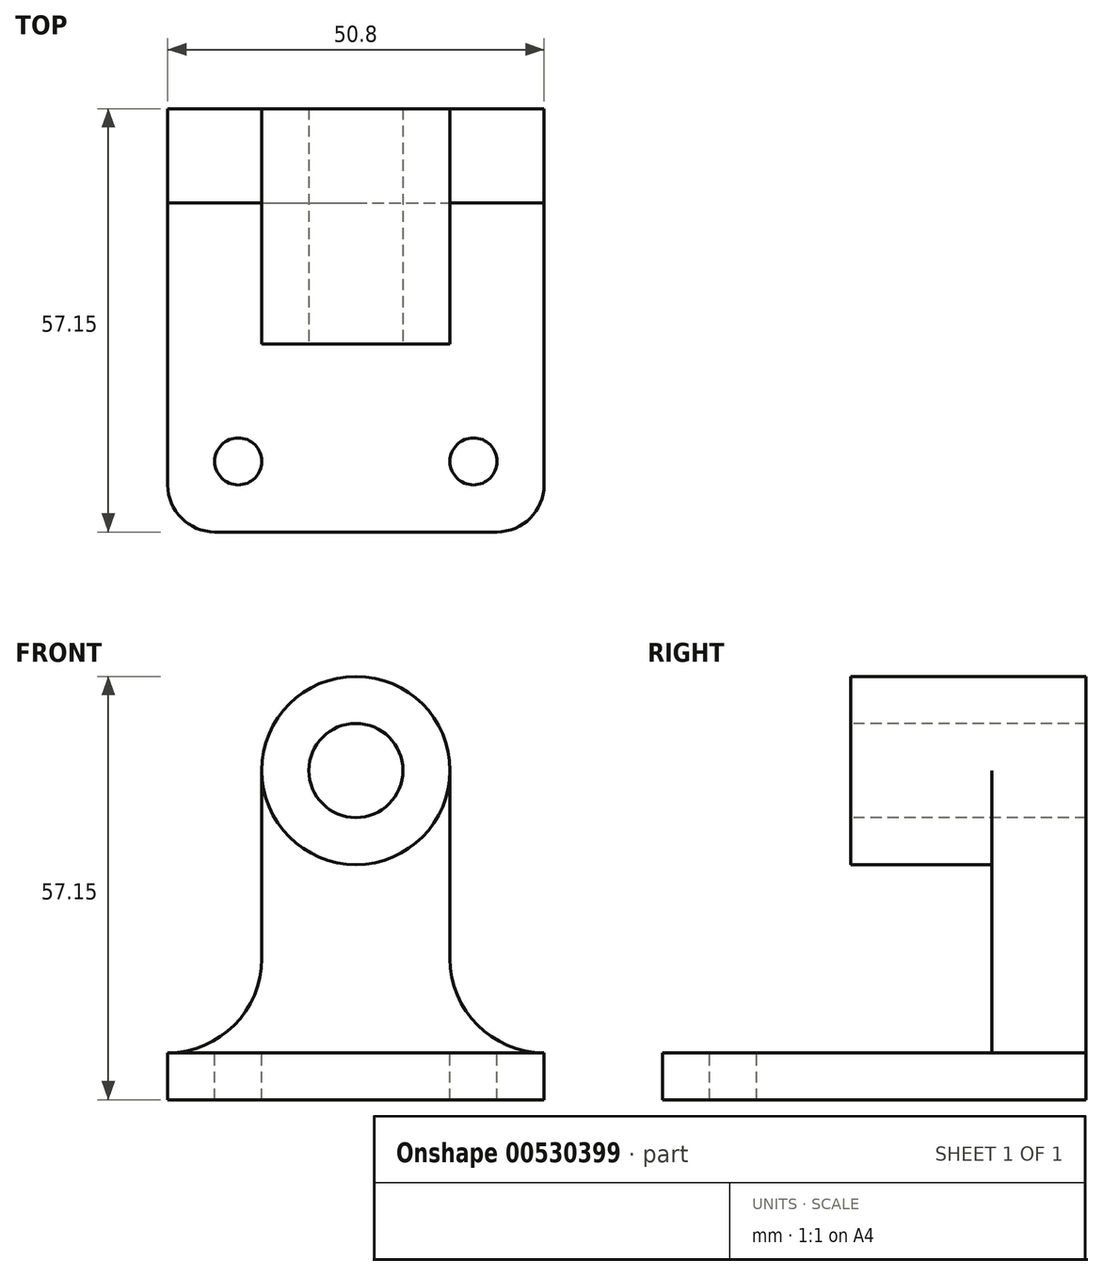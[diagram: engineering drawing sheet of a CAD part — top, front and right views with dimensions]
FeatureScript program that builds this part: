
annotation { "Feature Type Name" : "Feature", "Feature Type Description" : "" }
export const myFeature = defineFeature(function(context is Context, id is Id, definition is map)
    precondition{}
    {
        {
            var Q0;
            Q0=qCreatedBy(makeId("Front.planeOp"),FACE);
            var sketch = newSketch(context, id + "F0", { "sketchPlane" : qUnion([Q0])});
            skLineSegment(sketch, "E0.bottom", {"start": v(-66.92, 57.15) * mm, "end": v(-16.12, 57.15) * mm});
            skLineSegment(sketch, "E0.top", {"start": v(-66.92, 0) * mm, "end": v(-16.12, 0) * mm});
            skLineSegment(sketch, "E0.left", {"start": v(-66.92, 57.15) * mm, "end": v(-66.92, 0) * mm});
            skLineSegment(sketch, "E0.right", {"start": v(-16.12, 57.15) * mm, "end": v(-16.12, 0) * mm});
            skLineSegment(sketch, "E1", {"start": v(-66.92, 0) * mm, "end": v(-66.92, 6.35) * mm});
            skLineSegment(sketch, "E2", {"start": v(-66.92, 6.35) * mm, "end": v(-16.12, 6.35) * mm});
            skLineSegment(sketch, "E3", {"start": v(-16.12, 6.35) * mm, "end": v(-16.12, 0) * mm});
            skLineSegment(sketch, "E4", {"start": v(-66.92, 6.35) * mm, "end": v(-58.15, 6.35) * mm});
            skLineSegment(sketch, "E5", {"start": v(-58.15, 6.35) * mm, "end": v(-58.15, 57.15) * mm});
            skLineSegment(sketch, "E6", {"start": v(-58.15, 57.15) * mm, "end": v(-30.55, 57.15) * mm});
            skLineSegment(sketch, "E7", {"start": v(-30.55, 57.15) * mm, "end": v(-30.55, 6.35) * mm});
            skLineSegment(sketch, "E8", {"start": v(-30.55, 6.35) * mm, "end": v(-16.12, 6.35) * mm});
            skSolve(sketch);
        }
        {
            var Q0;
            Q0=makeQuery(id+"F0.imprint","IMPRINT",FACE,{"disambiguationData":[TD([[makeQuery(id+"F0.imprint","IMPRINT",EDGE,{"derivedFrom":sQuery(id+"F0.wireOp",EDGE,"E2")}),1.0]])]});
            var Q1;
            {var subQ0=sQuery(id+"F0.wireOp",EDGE,"E0.left");Q1=makeQuery(id+"F0.imprint","IMPRINT",FACE,{"disambiguationData":[TD([[makeQuery(id+"F0.imprint","IMPRINT",EDGE,{"derivedFrom":subQ0}),1.0]])]});}
            var Q2;
            {var subQ0=sQuery(id+"F0.wireOp",EDGE,"E0.right");Q2=makeQuery(id+"F0.imprint","IMPRINT",FACE,{"disambiguationData":[TD([[makeQuery(id+"F0.imprint","IMPRINT",EDGE,{"derivedFrom":subQ0}),-1.0]])]});}
            var Q3;
            Q3=makeQuery(id+"F0.imprint","IMPRINT",FACE,{"disambiguationData":[TD([[makeQuery(id+"F0.imprint","IMPRINT",EDGE,{"derivedFrom":sQuery(id+"F0.wireOp",EDGE,"E0.top")}),1.0]])]});
            extrude(context, id + "F1", {"entities" : qUnion([Q0, Q1, Q2, Q3]), "depth" : 31.75 * mm, "offsetDistance" : 25.4 * mm});
        }
        {
            var Q0;
            Q0=makeQuery(id+"F1.opExtrude","CAP_FACE",FACE,{"disambiguationData":[OSD([sQuery(id+"F0.wireOp",EDGE,"E0.bottom"),sQuery(id+"F0.wireOp",EDGE,"E0.top"),sQuery(id+"F0.wireOp",EDGE,"E0.left"),sQuery(id+"F0.wireOp",EDGE,"E0.right"),sQuery(id+"F0.wireOp",EDGE,"E1"),sQuery(id+"F0.wireOp",EDGE,"E3"),sQuery(id+"F0.wireOp",EDGE,"E6")])],"isStart":false});
            var sketch = newSketch(context, id + "F2", { "sketchPlane" : qUnion([Q0])});
            skLineSegment(sketch, "E9", {"start": v(-66.92, 0) * mm, "end": v(-66.92, 6.35) * mm});
            skLineSegment(sketch, "E10", {"start": v(-66.92, 6.35) * mm, "end": v(-16.12, 6.35) * mm});
            skLineSegment(sketch, "E11", {"start": v(-16.12, 6.35) * mm, "end": v(-16.12, 0) * mm});
            skLineSegment(sketch, "E12", {"start": v(-16.12, 0) * mm, "end": v(-66.92, 0) * mm});
            skLineSegment(sketch, "E13", {"start": v(-66.92, 6.35) * mm, "end": v(-66.92, 44.45) * mm});
            skLineSegment(sketch, "E14", {"start": v(-16.12, 44.45) * mm, "end": v(-16.12, 6.35) * mm});
            skCircle(sketch, "E15", {"center": v(-41.52, 44.45) * mm, "radius": 12.7 * mm});
            skCircle(sketch, "E16", {"center": v(-41.52, 44.45) * mm, "radius": 6.35 * mm});
            skLineSegment(sketch, "E17", {"start": v(-28.82, 44.45) * mm, "end": v(-28.82, 6.35) * mm});
            skLineSegment(sketch, "E18", {"start": v(-28.82, 6.35) * mm, "end": v(-16.12, 6.35) * mm});
            skLineSegment(sketch, "E19", {"start": v(-16.12, 44.45) * mm, "end": v(-28.82, 44.45) * mm});
            skLineSegment(sketch, "E20", {"start": v(-54.22, 44.45) * mm, "end": v(-54.22, 6.35) * mm});
            skLineSegment(sketch, "E21", {"start": v(-54.22, 6.35) * mm, "end": v(-66.92, 6.35) * mm});
            skLineSegment(sketch, "E22", {"start": v(-66.92, 44.45) * mm, "end": v(-54.22, 44.45) * mm});
            skLineSegment(sketch, "E23", {"start": v(-28.82, 44.45) * mm, "end": v(-16.12, 44.45) * mm});
            skLineSegment(sketch, "E24", {"start": v(-54.22, 44.45) * mm, "end": v(-28.82, 44.45) * mm});
            skLineSegment(sketch, "E25", {"start": v(-28.82, 44.45) * mm, "end": v(-28.82, 57.15) * mm});
            skLineSegment(sketch, "E26", {"start": v(-54.22, 44.45) * mm, "end": v(-54.22, 57.15) * mm});
            skLineSegment(sketch, "E27", {"start": v(-54.22, 57.15) * mm, "end": v(-66.92, 57.15) * mm});
            skLineSegment(sketch, "E28", {"start": v(-66.92, 57.15) * mm, "end": v(-66.92, 44.45) * mm});
            skLineSegment(sketch, "E29", {"start": v(-28.82, 57.15) * mm, "end": v(-16.12, 57.15) * mm});
            skLineSegment(sketch, "E30", {"start": v(-16.12, 57.15) * mm, "end": v(-16.12, 44.45) * mm});
            skSolve(sketch);
        }
        {
            var Q0;
            {var subQ3=sQuery(id+"F2.wireOp",EDGE,"E22");Q0=makeQuery(id+"F2.imprint","IMPRINT",FACE,{"disambiguationData":[TD([[makeQuery(id+"F2.imprint","IMPRINT",EDGE,{"derivedFrom":subQ3}),1.0]])]});}
            var Q1;
            {var subQ0=sQuery(id+"F2.wireOp",EDGE,"E26");var subQ1=sQuery(id+"F2.wireOp",EDGE,"E15");var subQ2=makeQuery(id+"F2.imprint","INTERSECT",VERTEX,{"derivedFrom":[subQ1,subQ0]});Q1=makeQuery(id+"F2.imprint","IMPRINT",FACE,{"disambiguationData":[TD([[makeQuery(id+"F2.imprint","IMPRINT",EDGE,{"disambiguationData":[TD([[subQ2,1.0]])],"derivedFrom":subQ1}),-1.0]])]});}
            var Q2;
            {var subQ0=sQuery(id+"F2.wireOp",EDGE,"E25");var subQ1=sQuery(id+"F2.wireOp",EDGE,"E15");var subQ2=makeQuery(id+"F2.imprint","INTERSECT",VERTEX,{"derivedFrom":[subQ1,subQ0]});Q2=makeQuery(id+"F2.imprint","IMPRINT",FACE,{"disambiguationData":[TD([[makeQuery(id+"F2.imprint","IMPRINT",EDGE,{"disambiguationData":[TD([[subQ2,-1.0]])],"derivedFrom":subQ1}),-1.0]])]});}
            var Q3;
            {var subQ3=sQuery(id+"F2.wireOp",EDGE,"E23");Q3=makeQuery(id+"F2.imprint","IMPRINT",FACE,{"disambiguationData":[TD([[makeQuery(id+"F2.imprint","IMPRINT",EDGE,{"derivedFrom":subQ3}),1.0]])]});}
            extrude(context, id + "F3", {"entities" : qUnion([Q0, Q1, Q2, Q3]), "operationType" : NewBodyOperationType.REMOVE, "endBound" : BoundingType.THROUGH_ALL, "oppositeDirection" : true, "depth" : 25.4 * mm, "offsetDistance" : 25.4 * mm});
        }
        {
            var Q0;
            Q0=makeQuery(id+"F1.opExtrude","CAP_FACE",FACE,{"disambiguationData":[OSD([sQuery(id+"F0.wireOp",EDGE,"E0.bottom"),sQuery(id+"F0.wireOp",EDGE,"E0.top"),sQuery(id+"F0.wireOp",EDGE,"E0.left"),sQuery(id+"F0.wireOp",EDGE,"E0.right"),sQuery(id+"F0.wireOp",EDGE,"E1"),sQuery(id+"F0.wireOp",EDGE,"E3"),sQuery(id+"F0.wireOp",EDGE,"E6")])],"isStart":false});
            var sketch = newSketch(context, id + "F4", { "sketchPlane" : qUnion([Q0])});
            skCircle(sketch, "E31", {"center": v(-41.52, 44.45) * mm, "radius": 12.7 * mm});
            skCircle(sketch, "E32", {"center": v(-41.52, 44.45) * mm, "radius": 6.35 * mm});
            skSolve(sketch);
        }
        {
            var Q0;
            Q0=makeQuery(id+"F4.imprint","IMPRINT",FACE,{"disambiguationData":[TD([[makeQuery(id+"F4.imprint","IMPRINT",EDGE,{"derivedFrom":sQuery(id+"F4.wireOp",EDGE,"E32")}),1.0]])]});
            extrude(context, id + "F5", {"entities" : qUnion([Q0]), "operationType" : NewBodyOperationType.REMOVE, "endBound" : BoundingType.THROUGH_ALL, "oppositeDirection" : true, "depth" : 25.4 * mm, "offsetDistance" : 25.4 * mm});
        }
        {
            var Q0;
            Q0 = qSketchRegion(id + "F4", true);
            extrude(context, id + "F6", {"entities" : qUnion([Q0]), "operationType" : NewBodyOperationType.REMOVE, "depth" : 12.7 * mm, "offsetDistance" : 25.4 * mm});
        }
        {
            var Q0;
            Q0=makeQuery(id+"F1.opExtrude","CAP_FACE",FACE,{"disambiguationData":[OSD([sQuery(id+"F0.wireOp",EDGE,"E0.bottom"),sQuery(id+"F0.wireOp",EDGE,"E0.top"),sQuery(id+"F0.wireOp",EDGE,"E0.left"),sQuery(id+"F0.wireOp",EDGE,"E0.right"),sQuery(id+"F0.wireOp",EDGE,"E1"),sQuery(id+"F0.wireOp",EDGE,"E3"),sQuery(id+"F0.wireOp",EDGE,"E6")])],"isStart":false});
            var sketch = newSketch(context, id + "F7", { "sketchPlane" : qUnion([Q0])});
            skLineSegment(sketch, "E33", {"start": v(-66.92, 0) * mm, "end": v(-66.92, 6.35) * mm});
            skLineSegment(sketch, "E34", {"start": v(-66.92, 6.35) * mm, "end": v(-16.12, 6.35) * mm});
            skLineSegment(sketch, "E35", {"start": v(-16.12, 6.35) * mm, "end": v(-16.12, 0) * mm});
            skLineSegment(sketch, "E36", {"start": v(-16.12, 0) * mm, "end": v(-66.92, 0) * mm});
            skLineSegment(sketch, "E37", {"start": v(-28.82, 44.45) * mm, "end": v(-28.82, 19.05) * mm});
            skLineSegment(sketch, "E38", {"start": v(-28.82, 19.05) * mm, "end": v(-28.82, 6.35) * mm});
            skLineSegment(sketch, "E39", {"start": v(-54.22, 44.45) * mm, "end": v(-54.22, 19.05) * mm});
            skLineSegment(sketch, "E40", {"start": v(-54.22, 19.05) * mm, "end": v(-54.22, 6.35) * mm});
            skArc(sketch, "E41", {"start": v(-66.92, 6.35) * mm, "mid": v(-57.94, 10.07) * mm, "end": v(-54.22, 19.05) * mm});
            skArc(sketch, "E42", {"start": v(-28.82, 19.05) * mm, "mid": v(-25.1, 10.07) * mm, "end": v(-16.12, 6.35) * mm});
            skSolve(sketch);
        }
        {
            var Q0;
            Q0=makeQuery(id+"F7.imprint","IMPRINT",FACE,{"disambiguationData":[TD([[makeQuery(id+"F7.imprint","IMPRINT",EDGE,{"derivedFrom":sQuery(id+"F7.wireOp",EDGE,"E39")}),-1.0]])]});
            var Q1;
            Q1=makeQuery(id+"F7.imprint","IMPRINT",FACE,{"disambiguationData":[TD([[makeQuery(id+"F7.imprint","IMPRINT",EDGE,{"derivedFrom":sQuery(id+"F7.wireOp",EDGE,"E37")}),1.0]])]});
            extrude(context, id + "F8", {"entities" : qUnion([Q0, Q1]), "operationType" : NewBodyOperationType.REMOVE, "endBound" : BoundingType.THROUGH_ALL, "oppositeDirection" : true, "depth" : 25.4 * mm, "offsetDistance" : 25.4 * mm});
        }
        {
            var Q0;
            Q0=makeQuery(id+"F1.opExtrude","CAP_FACE",FACE,{"disambiguationData":[OSD([sQuery(id+"F0.wireOp",EDGE,"E0.bottom"),sQuery(id+"F0.wireOp",EDGE,"E0.top"),sQuery(id+"F0.wireOp",EDGE,"E0.left"),sQuery(id+"F0.wireOp",EDGE,"E0.right"),sQuery(id+"F0.wireOp",EDGE,"E1"),sQuery(id+"F0.wireOp",EDGE,"E3"),sQuery(id+"F0.wireOp",EDGE,"E6")])],"isStart":false});
            var sketch = newSketch(context, id + "F9", { "sketchPlane" : qUnion([Q0])});
            skLineSegment(sketch, "E43", {"start": v(-66.92, 6.35) * mm, "end": v(-16.12, 6.35) * mm});
            skArc(sketch, "E44", {"start": v(-66.92, 6.35) * mm, "mid": v(-57.94, 10.07) * mm, "end": v(-54.22, 19.05) * mm});
            skArc(sketch, "E45", {"start": v(-28.82, 19.05) * mm, "mid": v(-25.1, 10.07) * mm, "end": v(-16.12, 6.35) * mm});
            skArc(sketch, "E46", {"start": v(-54.22, 44.45) * mm, "mid": v(-41.52, 31.75) * mm, "end": v(-28.82, 44.45) * mm});
            skLineSegment(sketch, "E47", {"start": v(-54.22, 44.45) * mm, "end": v(-54.22, 19.05) * mm});
            skLineSegment(sketch, "E48", {"start": v(-28.82, 44.45) * mm, "end": v(-28.82, 19.05) * mm});
            skSolve(sketch);
        }
        {
            var Q0;
            Q0=makeQuery(id+"F9.imprint","IMPRINT",FACE,{"disambiguationData":[TD([[makeQuery(id+"F9.imprint","IMPRINT",EDGE,{"derivedFrom":sQuery(id+"F9.wireOp",EDGE,"E43")}),1.0]])]});
            extrude(context, id + "F10", {"entities" : qUnion([Q0]), "operationType" : NewBodyOperationType.REMOVE, "oppositeDirection" : true, "depth" : 19.05 * mm, "offsetDistance" : 25.4 * mm});
        }
        {
            var Q0;
            {var subQ0=sQuery(id+"F0.wireOp",EDGE,"E0.top");var subQ1=sQuery(id+"F0.wireOp",EDGE,"E1");var subQ2=sQuery(id+"F0.wireOp",EDGE,"E0.left");var subQ3=sQuery(id+"F0.wireOp",EDGE,"E3");var subQ4=sQuery(id+"F0.wireOp",EDGE,"E0.right");Q0=makeQuery(id+"F10.boolean.opBoolean","SPLIT",FACE,{"disambiguationData":[TD([makeQuery(id+"F1.opExtrude","SWEPT_FACE",FACE,{"disambiguationData":[OSD([subQ0])]})])],"derivedFrom":makeQuery(id+"F1.opExtrude","CAP_FACE",FACE,{"disambiguationData":[OSD([sQuery(id+"F0.wireOp",EDGE,"E0.bottom"),subQ0,subQ2,subQ4,subQ1,subQ3,sQuery(id+"F0.wireOp",EDGE,"E6")])],"isStart":false})});}
            extrude(context, id + "F11", {"entities" : qUnion([Q0]), "operationType" : NewBodyOperationType.ADD, "depth" : 25.4 * mm, "offsetDistance" : 25.4 * mm});
        }
        {
            var Q0;
            {var subQ0=sQuery(id+"F9.wireOp",EDGE,"E43");Q0=makeQuery(id+"F11.boolean.opBoolean","MERGE",FACE,{"derivedFrom":[makeQuery(id+"F10.boolean.opBoolean","COPY",FACE,{"derivedFrom":makeQuery(id+"F10.opExtrude","SWEPT_FACE",FACE,{"disambiguationData":[OSD([subQ0])]})}),makeQuery(id+"F11.opExtrude","SWEPT_FACE",FACE,{"disambiguationData":[OSD([subQ0])]})]});}
            var sketch = newSketch(context, id + "F12", { "sketchPlane" : qUnion([Q0])});
            skLineSegment(sketch, "E49", {"start": v(-66.92, -57.15) * mm, "end": v(-66.92, -50.8) * mm});
            skLineSegment(sketch, "E50", {"start": v(-66.92, -50.8) * mm, "end": v(-60.57, -50.8) * mm});
            skLineSegment(sketch, "E51", {"start": v(-60.57, -50.8) * mm, "end": v(-60.57, -57.15) * mm});
            skLineSegment(sketch, "E52", {"start": v(-60.57, -57.15) * mm, "end": v(-66.92, -57.15) * mm});
            skLineSegment(sketch, "E53", {"start": v(-22.47, -57.15) * mm, "end": v(-22.47, -50.8) * mm});
            skLineSegment(sketch, "E54", {"start": v(-22.47, -50.8) * mm, "end": v(-16.12, -50.8) * mm});
            skLineSegment(sketch, "E55", {"start": v(-16.12, -50.8) * mm, "end": v(-16.12, -57.15) * mm});
            skLineSegment(sketch, "E56", {"start": v(-16.12, -57.15) * mm, "end": v(-22.47, -57.15) * mm});
            skArc(sketch, "E57", {"start": v(-66.92, -50.8) * mm, "mid": v(-65.06, -55.3) * mm, "end": v(-60.57, -57.15) * mm});
            skArc(sketch, "E58", {"start": v(-22.47, -57.15) * mm, "mid": v(-17.98, -55.3) * mm, "end": v(-16.12, -50.8) * mm});
            skSolve(sketch);
        }
        {
            var Q0;
            Q0=makeQuery(id+"F12.imprint","IMPRINT",FACE,{"disambiguationData":[TD([[makeQuery(id+"F12.imprint","IMPRINT",EDGE,{"derivedFrom":sQuery(id+"F12.wireOp",EDGE,"E49")}),1.0]])]});
            var Q1;
            Q1=makeQuery(id+"F12.imprint","IMPRINT",FACE,{"disambiguationData":[TD([[makeQuery(id+"F12.imprint","IMPRINT",EDGE,{"derivedFrom":sQuery(id+"F12.wireOp",EDGE,"E55")}),-1.0]])]});
            extrude(context, id + "F13", {"entities" : qUnion([Q0, Q1]), "operationType" : NewBodyOperationType.REMOVE, "endBound" : BoundingType.THROUGH_ALL, "oppositeDirection" : true, "depth" : 25.4 * mm, "offsetDistance" : 25.4 * mm});
        }
        {
            var Q0;
            {var subQ0=sQuery(id+"F9.wireOp",EDGE,"E43");Q0=makeQuery(id+"F11.boolean.opBoolean","MERGE",FACE,{"derivedFrom":[makeQuery(id+"F10.boolean.opBoolean","COPY",FACE,{"derivedFrom":makeQuery(id+"F10.opExtrude","SWEPT_FACE",FACE,{"disambiguationData":[OSD([subQ0])]})}),makeQuery(id+"F11.opExtrude","SWEPT_FACE",FACE,{"disambiguationData":[OSD([subQ0])]})]});}
            var sketch = newSketch(context, id + "F14", { "sketchPlane" : qUnion([Q0])});
            skCircle(sketch, "E59", {"center": v(-57.4, -47.63) * mm, "radius": 3.18 * mm});
            skCircle(sketch, "E60", {"center": v(-25.65, -47.63) * mm, "radius": 3.18 * mm});
            skSolve(sketch);
        }
        {
            var Q0;
            Q0=makeQuery(id+"F14.imprint","IMPRINT",FACE,{"disambiguationData":[TD([[makeQuery(id+"F14.imprint","IMPRINT",EDGE,{"derivedFrom":sQuery(id+"F14.wireOp",EDGE,"E59")}),1.0]])]});
            var Q1;
            Q1=makeQuery(id+"F14.imprint","IMPRINT",FACE,{"disambiguationData":[TD([[makeQuery(id+"F14.imprint","IMPRINT",EDGE,{"derivedFrom":sQuery(id+"F14.wireOp",EDGE,"E60")}),1.0]])]});
            extrude(context, id + "F15", {"entities" : qUnion([Q0, Q1]), "operationType" : NewBodyOperationType.REMOVE, "endBound" : BoundingType.THROUGH_ALL, "oppositeDirection" : true, "depth" : 25.4 * mm, "offsetDistance" : 25.4 * mm});
        }
    });
